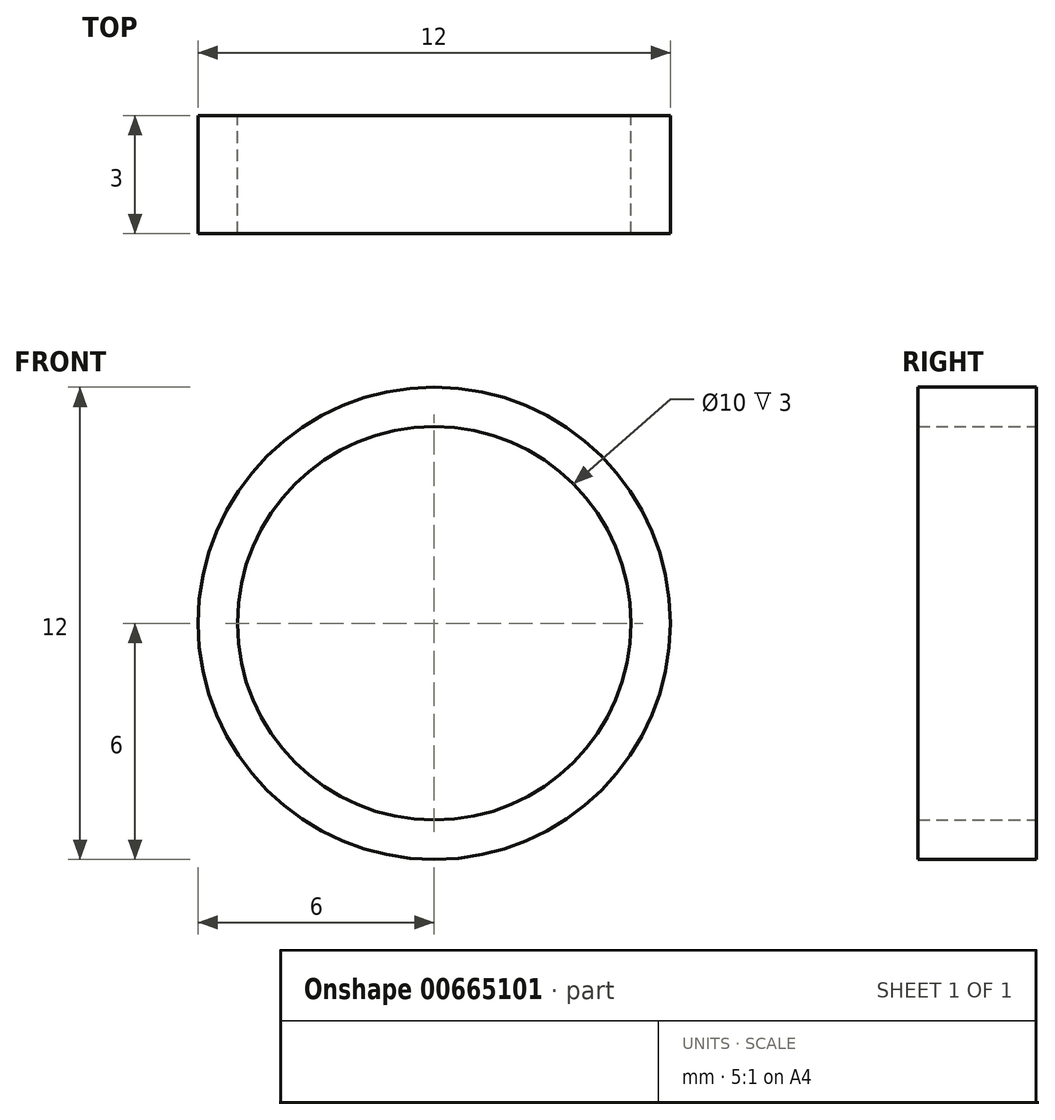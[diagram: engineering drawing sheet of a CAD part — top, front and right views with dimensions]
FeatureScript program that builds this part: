
annotation { "Feature Type Name" : "Feature", "Feature Type Description" : "" }
export const myFeature = defineFeature(function(context is Context, id is Id, definition is map)
    precondition{}
    {
        {
            var Q0;
            Q0=qCreatedBy(makeId("Front.planeOp"),FACE);
            var sketch = newSketch(context, id + "F0", { "sketchPlane" : qUnion([Q0])});
            skCircle(sketch, "E0", {"center": v(0, 0) * mm, "radius": 5 * mm});
            skCircle(sketch, "E1", {"center": v(0, 0) * mm, "radius": 6 * mm});
            skSolve(sketch);
        }
        {
            var Q0;
            Q0 = qSketchRegion(id + "F0", true);
            extrude(context, id + "F1", {"entities" : qUnion([Q0]), "depth" : 3 * mm, "offsetDistance" : 25 * mm});
        }
    });
